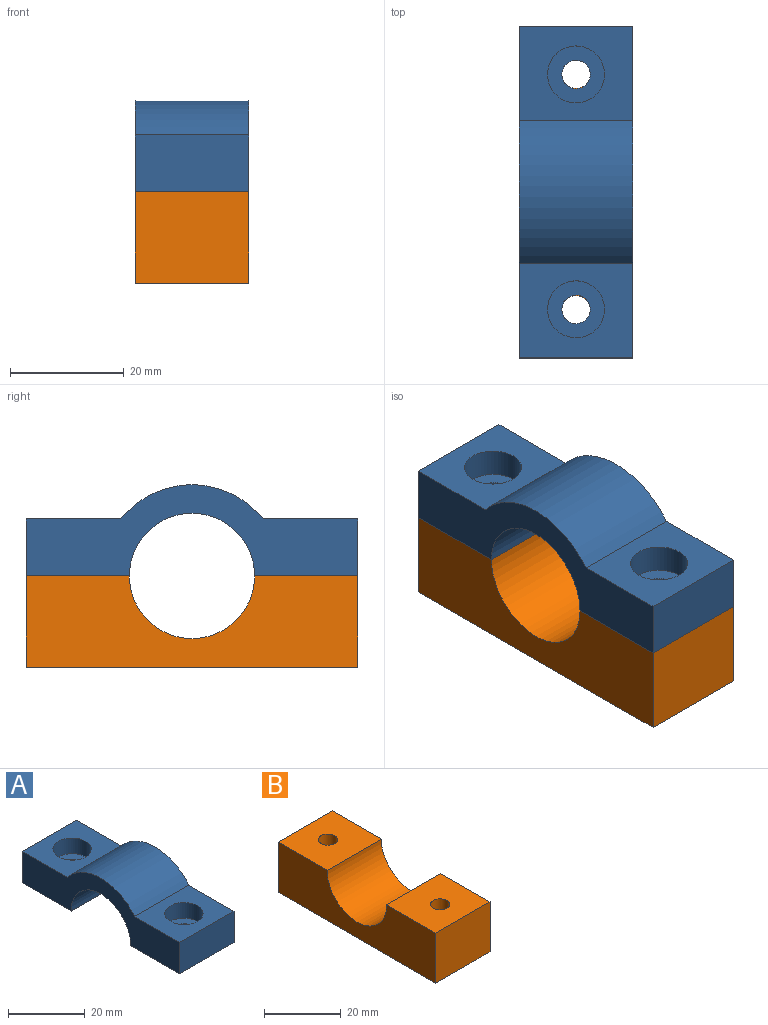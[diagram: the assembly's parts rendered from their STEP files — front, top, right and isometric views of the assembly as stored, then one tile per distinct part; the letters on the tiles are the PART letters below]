
ASSEMBLY  parts=2 mates=1
PART A: 16 faces, bbox 20x58.3x16 mm
  f0: plane 20x16.64mm, normal (0,0,1), area 254.2mm2, adj f1,f7,f8,f9,f13
  f1: cylinder r=16mm len=24.98mm, axis (-1,0,0), area 573.2mm2, adj f0,f2,f8,f9
  f2: plane 20x16.64mm, normal (0,0,1), area 254.2mm2, adj f1,f3,f8,f9,f10
  f3: plane 20x10mm, normal (0,-1,0), area 200mm2, adj f2,f4,f8,f9
  f4: plane 20x18.13mm, normal (0,0,-1), area 342.9mm2, adj f3,f5,f8,f9,f12
  f5: cylinder r=11mm len=22mm, axis (-1,0,0), area 691.2mm2, adj f4,f6,f8,f9
  f6: plane 20x18.13mm, normal (0,0,-1), area 342.9mm2, adj f5,f7,f8,f9,f15
  f7: plane 20x10mm, normal (0,1,0), area 200mm2, adj f0,f6,f8,f9
  f8: plane 58.25x16mm, normal (1,0,0), area 496.8mm2, adj f0,f1,f2,f3,f4,f5,f6,f7
  f9: plane 58.25x16mm, normal (-1,0,0), area 496.8mm2, adj f0,f1,f2,f3,f4,f5,f6,f7
  f10: cylinder r=5mm len=10mm, axis (0,0,1), area 157.1mm2, adj f2,f11
  f11: plane 10x10mm, normal (0,0,1), area 58.9mm2, adj f10,f12
  f12: cylinder r=2.5mm len=5mm, axis (0,0,1), area 78.5mm2, adj f4,f11
  f13: cylinder r=5mm len=10mm, axis (0,0,1), area 157.1mm2, adj f0,f14
  f14: plane 10x10mm, normal (0,0,1), area 58.9mm2, adj f13,f15
  f15: cylinder r=2.5mm len=5mm, axis (0,0,1), area 78.5mm2, adj f6,f14
PART B: 10 faces, bbox 20x58.3x16 mm
  f0: cylinder r=11mm len=22mm, axis (1,0,0), area 691.2mm2, adj f1,f4,f5,f7
  f1: plane 20x18.13mm, normal (0,0,1), area 342.9mm2, adj f0,f2,f4,f5,f6
  f2: plane 20x16mm, normal (0,-1,0), area 320mm2, adj f1,f3,f4,f5
  f3: plane 58.25x20mm, normal (0,0,-1), area 1125.7mm2, adj f2,f4,f5,f6,f8,f9
  f4: plane 58.25x16mm, normal (-1,0,0), area 741.9mm2, adj f0,f1,f2,f3,f7,f8
  f5: plane 58.25x16mm, normal (1,0,0), area 741.9mm2, adj f0,f1,f2,f3,f7,f8
  f6: cylinder r=2.5mm len=16mm, axis (0,0,1), area 251.3mm2, adj f1,f3
  f7: plane 20x18.13mm, normal (0,0,1), area 342.9mm2, adj f0,f4,f5,f8,f9
  f8: plane 20x16mm, normal (0,1,0), area 320mm2, adj f3,f4,f5,f7
  f9: cylinder r=2.5mm len=16mm, axis (0,0,1), area 251.3mm2, adj f3,f7
PLACE A t=(-30.52,-13.78,5.09)mm
PLACE B t=(-10.52,-13.78,5.09)mm fixed
MATE fastened A.f4 <-> B.f1  axis (0,0,1) through (-10.52,-42.91,5.09)mm
